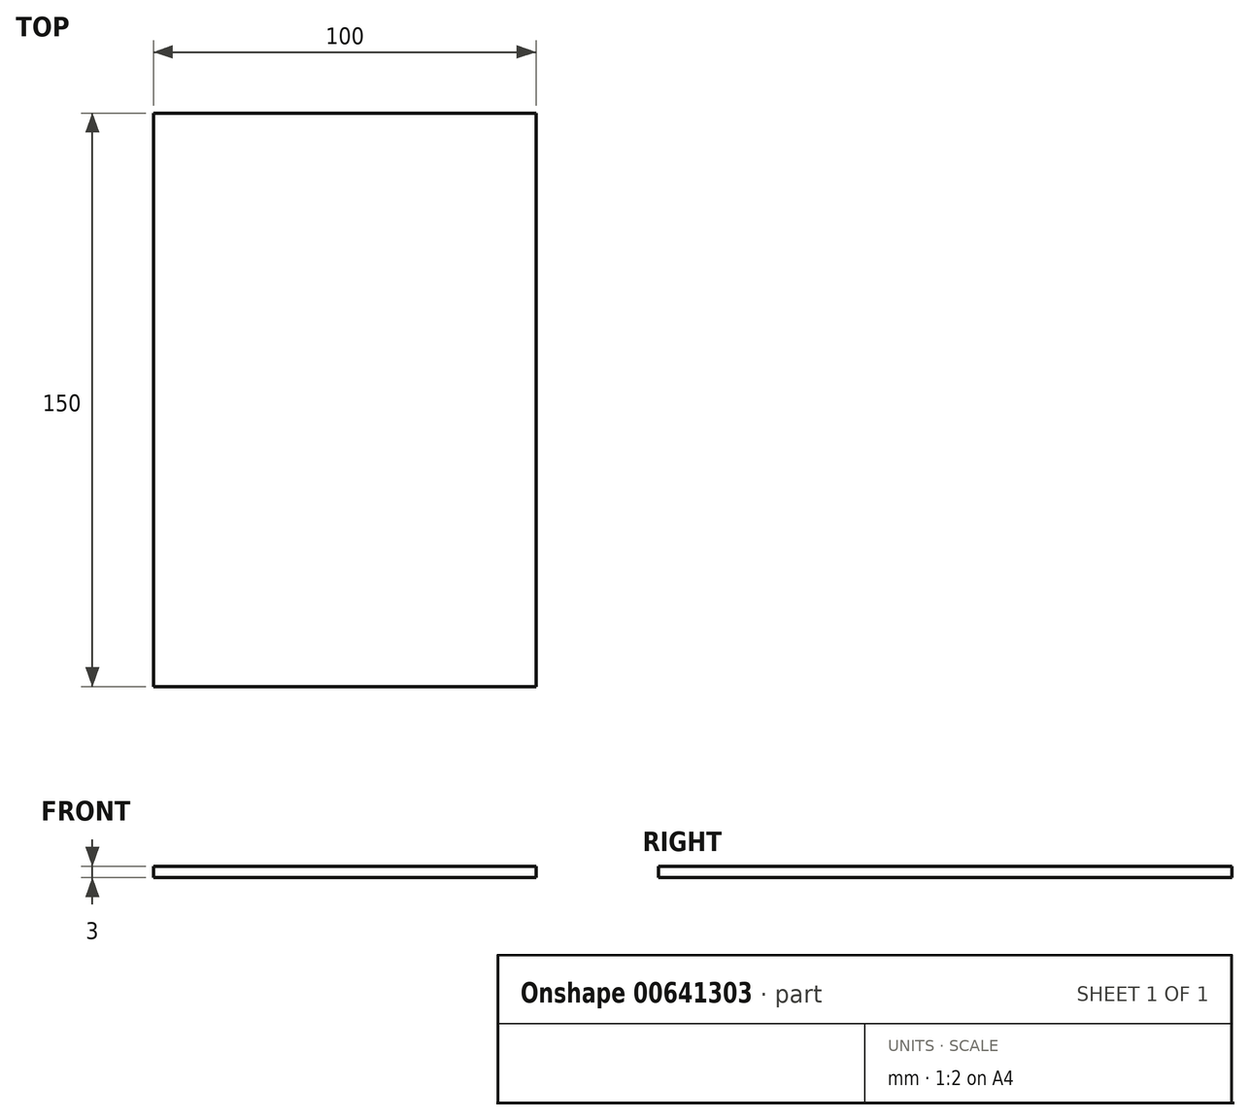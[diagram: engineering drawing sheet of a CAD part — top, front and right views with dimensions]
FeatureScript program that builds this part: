
annotation { "Feature Type Name" : "Feature", "Feature Type Description" : "" }
export const myFeature = defineFeature(function(context is Context, id is Id, definition is map)
    precondition{}
    {
        {
            var Q0;
            Q0=qCreatedBy(makeId("Top.planeOp"),FACE);
            var sketch = newSketch(context, id + "F0", { "sketchPlane" : qUnion([Q0])});
            skLineSegment(sketch, "E0.bottom", {"start": v(25.5, 0) * mm, "end": v(-74.5, 0) * mm});
            skLineSegment(sketch, "E0.top", {"start": v(25.5, 150) * mm, "end": v(-74.5, 150) * mm});
            skLineSegment(sketch, "E0.left", {"start": v(25.5, 0) * mm, "end": v(25.5, 150) * mm});
            skLineSegment(sketch, "E0.right", {"start": v(-74.5, 0) * mm, "end": v(-74.5, 150) * mm});
            skSolve(sketch);
        }
        {
            var Q0;
            Q0=makeQuery(id+"F0.imprint","IMPRINT",FACE,{"disambiguationData":[TD([[makeQuery(id+"F0.imprint","IMPRINT",EDGE,{"derivedFrom":sQuery(id+"F0.wireOp",EDGE,"E0.bottom")}),-1.0]])]});
            extrude(context, id + "F1", {"entities" : qUnion([Q0]), "depth" : 3 * mm, "offsetDistance" : 25 * mm});
        }
    });
